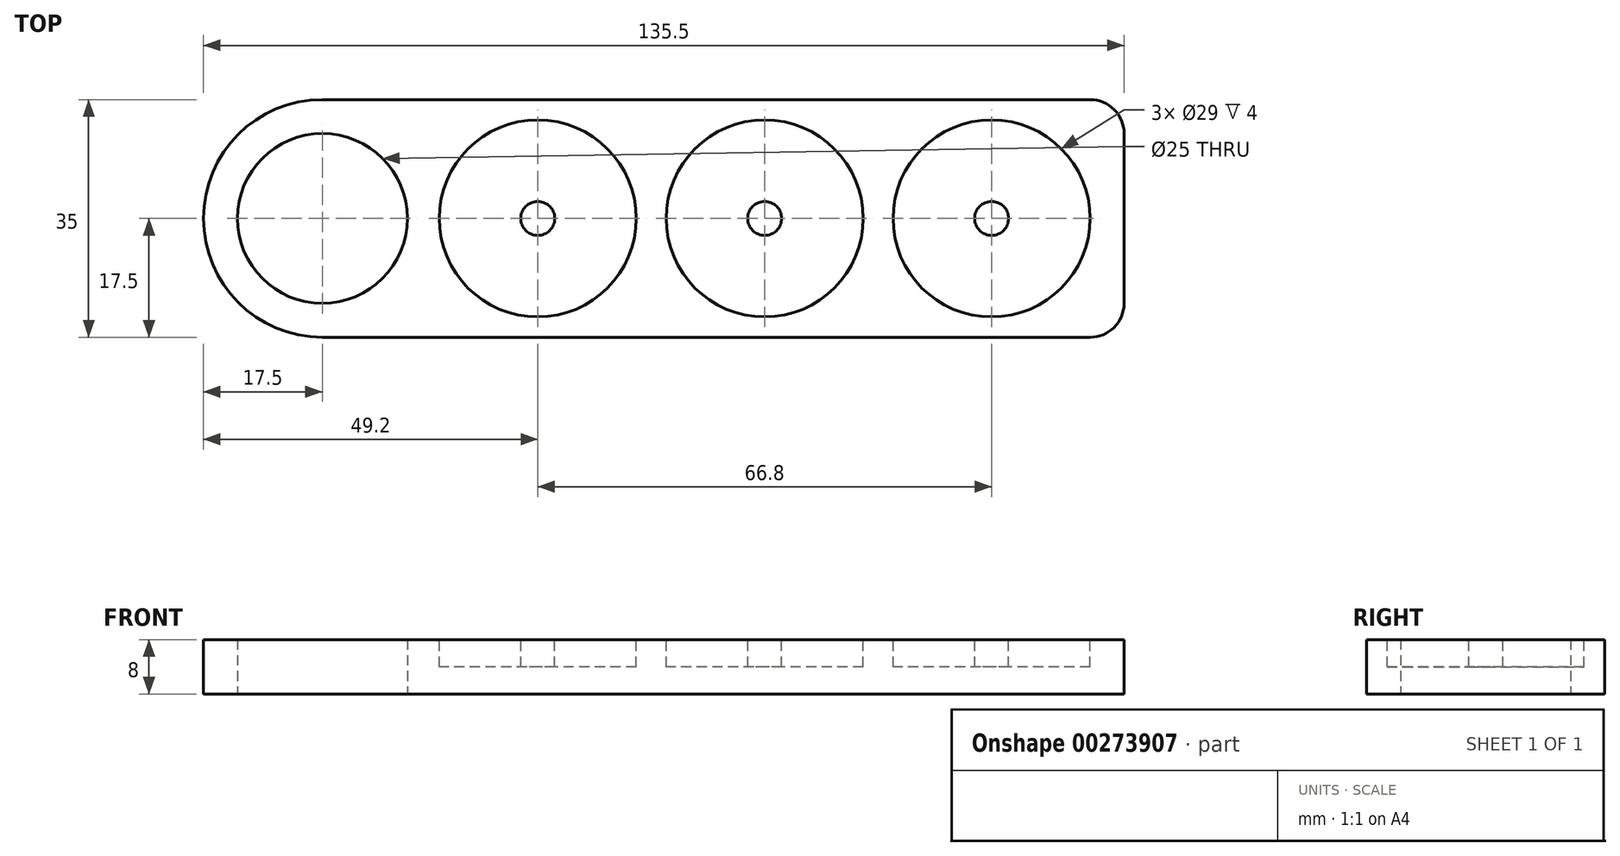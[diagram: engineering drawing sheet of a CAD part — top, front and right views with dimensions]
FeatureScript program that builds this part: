
annotation { "Feature Type Name" : "Feature", "Feature Type Description" : "" }
export const myFeature = defineFeature(function(context is Context, id is Id, definition is map)
    precondition{}
    {
        {
            var Q0;
            Q0=qCreatedBy(makeId("Top.planeOp"),FACE);
            var sketch = newSketch(context, id + "F0", { "sketchPlane" : qUnion([Q0])});
            skLineSegment(sketch, "E0.bottom", {"start": v(17.5, 0) * mm, "end": v(130.5, 0) * mm});
            skLineSegment(sketch, "E0.top", {"start": v(17.5, 35) * mm, "end": v(130.5, 35) * mm});
            skLineSegment(sketch, "E0.left", {"start": v(0, 17.5) * mm, "end": v(0, 17.5) * mm});
            skLineSegment(sketch, "E0.right", {"start": v(135.5, 5) * mm, "end": v(135.5, 30) * mm});
            skLineSegment(sketch, "E1.bottom", {"start": v(0, 0) * mm, "end": v(17.5, 0) * mm, "construction": true});
            skLineSegment(sketch, "E1.top", {"start": v(0, 17.5) * mm, "end": v(17.5, 17.5) * mm, "construction": true});
            skLineSegment(sketch, "E1.left", {"start": v(0, 0) * mm, "end": v(0, 17.5) * mm, "construction": true});
            skLineSegment(sketch, "E1.right", {"start": v(17.5, 0) * mm, "end": v(17.5, 17.5) * mm, "construction": true});
            skCircle(sketch, "E2", {"center": v(17.5, 17.5) * mm, "radius": 12.5 * mm});
            skPoint(sketch, "E3.visualSharp", {"position": v(0, 0) * mm});
            skArc(sketch, "E3.filletArc", {"start": v(0, 17.5) * mm, "mid": v(5.13, 5.13) * mm, "end": v(17.5, 0) * mm});
            skPoint(sketch, "E4.visualSharp", {"position": v(0, 35) * mm});
            skArc(sketch, "E4.filletArc", {"start": v(17.5, 35) * mm, "mid": v(5.13, 29.87) * mm, "end": v(0, 17.5) * mm});
            skPoint(sketch, "E5.visualSharp", {"position": v(135.5, 35) * mm});
            skArc(sketch, "E5.filletArc", {"start": v(135.5, 30) * mm, "mid": v(134.04, 33.54) * mm, "end": v(130.5, 35) * mm});
            skPoint(sketch, "E6.visualSharp", {"position": v(135.5, 0) * mm});
            skArc(sketch, "E6.filletArc", {"start": v(130.5, 0) * mm, "mid": v(134.04, 1.46) * mm, "end": v(135.5, 5) * mm});
            skSolve(sketch);
        }
        {
            var Q0;
            Q0=makeQuery(id+"F0.imprint","IMPRINT",FACE,{"disambiguationData":[TD([[makeQuery(id+"F0.imprint","IMPRINT",EDGE,{"derivedFrom":sQuery(id+"F0.wireOp",EDGE,"E0.bottom")}),1.0]])]});
            extrude(context, id + "F1", {"entities" : qUnion([Q0]), "depth" : 8 * mm});
        }
        {
            var Q0;
            Q0=makeQuery(id+"F1.opExtrude","CAP_FACE",FACE,{"disambiguationData":[OSD([sQuery(id+"F0.wireOp",EDGE,"E0.bottom"),sQuery(id+"F0.wireOp",EDGE,"E0.top"),sQuery(id+"F0.wireOp",EDGE,"E0.right"),sQuery(id+"F0.wireOp",EDGE,"E2"),sQuery(id+"F0.wireOp",EDGE,"E3.filletArc"),sQuery(id+"F0.wireOp",EDGE,"E4.filletArc"),sQuery(id+"F0.wireOp",EDGE,"E5.filletArc"),sQuery(id+"F0.wireOp",EDGE,"E6.filletArc")])],"isStart":false});
            var sketch = newSketch(context, id + "F2", { "sketchPlane" : qUnion([Q0])});
            skLineSegment(sketch, "E7.bottom", {"start": v(0, 0) * mm, "end": v(49.2, 0) * mm, "construction": true});
            skLineSegment(sketch, "E7.top", {"start": v(0, 17.5) * mm, "end": v(49.2, 17.5) * mm, "construction": true});
            skLineSegment(sketch, "E7.left", {"start": v(0, 0) * mm, "end": v(0, 17.5) * mm, "construction": true});
            skLineSegment(sketch, "E7.right", {"start": v(49.2, 0) * mm, "end": v(49.2, 17.5) * mm, "construction": true});
            skLineSegment(sketch, "E8", {"start": v(49.2, 17.5) * mm, "end": v(82.6, 17.5) * mm, "construction": true});
            skLineSegment(sketch, "E9", {"start": v(82.6, 17.5) * mm, "end": v(116, 17.5) * mm, "construction": true});
            skCircle(sketch, "E10", {"center": v(49.2, 17.5) * mm, "radius": 14.5 * mm});
            skCircle(sketch, "E11", {"center": v(82.6, 17.5) * mm, "radius": 14.5 * mm});
            skCircle(sketch, "E12", {"center": v(116, 17.5) * mm, "radius": 14.5 * mm});
            skCircle(sketch, "E13", {"center": v(116, 17.5) * mm, "radius": 2.5 * mm});
            skCircle(sketch, "E14", {"center": v(82.6, 17.5) * mm, "radius": 2.5 * mm});
            skCircle(sketch, "E15", {"center": v(49.2, 17.5) * mm, "radius": 2.5 * mm});
            skSolve(sketch);
        }
        {
            var Q0;
            Q0=makeQuery(id+"F2.imprint","IMPRINT",FACE,{"disambiguationData":[TD([[makeQuery(id+"F2.imprint","IMPRINT",EDGE,{"derivedFrom":sQuery(id+"F2.wireOp",EDGE,"E10")}),1.0]])]});
            var Q1;
            Q1=makeQuery(id+"F2.imprint","IMPRINT",FACE,{"disambiguationData":[TD([[makeQuery(id+"F2.imprint","IMPRINT",EDGE,{"derivedFrom":sQuery(id+"F2.wireOp",EDGE,"E11")}),1.0]])]});
            var Q2;
            Q2=makeQuery(id+"F2.imprint","IMPRINT",FACE,{"disambiguationData":[TD([[makeQuery(id+"F2.imprint","IMPRINT",EDGE,{"derivedFrom":sQuery(id+"F2.wireOp",EDGE,"E12")}),1.0]])]});
            extrude(context, id + "F3", {"entities" : qUnion([Q0, Q1, Q2]), "operationType" : NewBodyOperationType.REMOVE, "oppositeDirection" : true, "depth" : 4 * mm});
        }
    });
